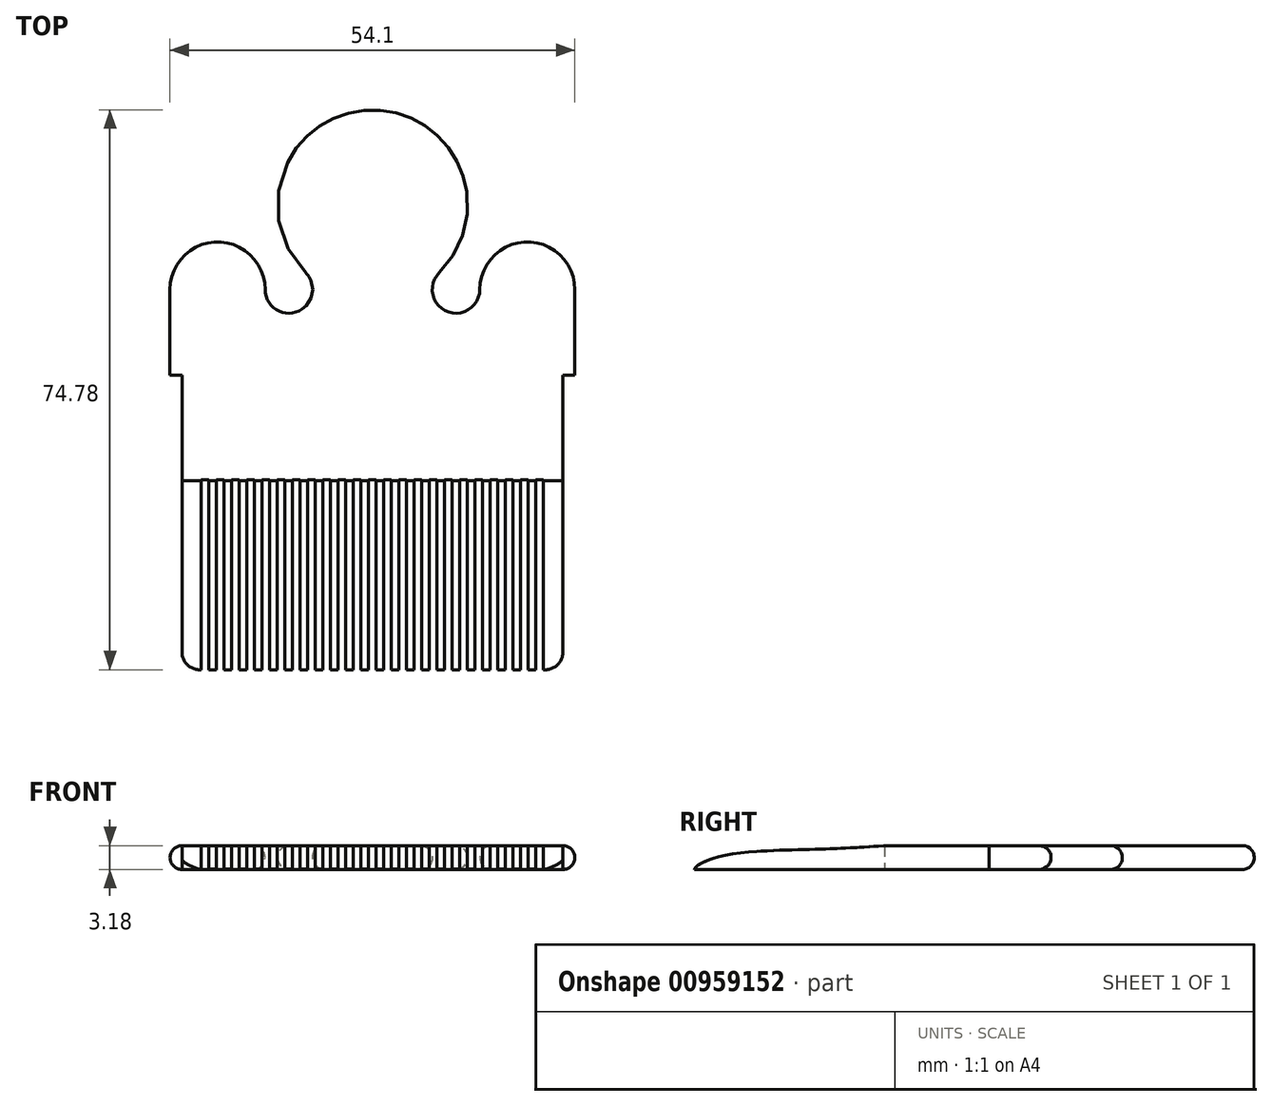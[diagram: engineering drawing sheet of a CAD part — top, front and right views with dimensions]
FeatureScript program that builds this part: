
annotation { "Feature Type Name" : "Feature", "Feature Type Description" : "" }
export const myFeature = defineFeature(function(context is Context, id is Id, definition is map)
    precondition{}
    {
        {
            var Q0;
            Q0=qCreatedBy(makeId("Top.planeOp"),FACE);
            var sketch = newSketch(context, id + "F0", { "sketchPlane" : qUnion([Q0])});
            skPoint(sketch, "E0.middle", {"position": v(0, 0) * mm});
            skArc(sketch, "E1", {"start": v(8.94, 27.66) * mm, "mid": v(0, 49.38) * mm, "end": v(-8.94, 27.66) * mm});
            skArc(sketch, "E2", {"start": v(8.94, 27.66) * mm, "mid": v(9.95, 22.47) * mm, "end": v(14.35, 25.4) * mm});
            skArc(sketch, "E3", {"start": v(-14.35, 25.4) * mm, "mid": v(-9.95, 22.47) * mm, "end": v(-8.94, 27.66) * mm});
            skArc(sketch, "E4", {"start": v(27.05, 25.4) * mm, "mid": v(20.7, 31.75) * mm, "end": v(14.35, 25.4) * mm});
            skArc(sketch, "E5", {"start": v(-14.35, 25.4) * mm, "mid": v(-20.7, 31.75) * mm, "end": v(-27.05, 25.4) * mm});
            skLineSegment(sketch, "E6.bottom", {"start": v(27.05, 25.4) * mm, "end": v(27.05, 25.4) * mm});
            skLineSegment(sketch, "E7.bottom", {"start": v(-27.05, 25.4) * mm, "end": v(-27.05, 25.4) * mm});
            skLineSegment(sketch, "E8", {"start": v(25.45, 13.97) * mm, "end": v(27.05, 13.97) * mm});
            skLineSegment(sketch, "E9", {"start": v(-25.45, 13.97) * mm, "end": v(-27.05, 13.97) * mm});
            skLineSegment(sketch, "E10.trimOffspring", {"start": v(17.78, -25.4) * mm, "end": v(16.76, -25.4) * mm});
            skLineSegment(sketch, "E11.top", {"start": v(-0.5, 0) * mm, "end": v(0.5, 0) * mm});
            skLineSegment(sketch, "E11.left", {"start": v(-0.5, -25.4) * mm, "end": v(-0.5, 0) * mm});
            skLineSegment(sketch, "E11.right", {"start": v(0.5, -25.4) * mm, "end": v(0.5, 0) * mm});
            skLineSegment(sketch, "E12.0", {"start": v(1.52, -25.4) * mm, "end": v(1.52, 0) * mm});
            skLineSegment(sketch, "E13.0", {"start": v(2.54, -25.4) * mm, "end": v(2.54, 0) * mm});
            skLineSegment(sketch, "E14.0", {"start": v(3.56, -25.4) * mm, "end": v(3.56, 0) * mm});
            skLineSegment(sketch, "E15.0", {"start": v(4.57, -25.4) * mm, "end": v(4.57, 0) * mm});
            skLineSegment(sketch, "E16.0", {"start": v(5.59, -25.4) * mm, "end": v(5.59, 0) * mm});
            skLineSegment(sketch, "E17.0", {"start": v(6.6, -25.4) * mm, "end": v(6.6, 0) * mm});
            skLineSegment(sketch, "E18.0", {"start": v(7.62, -25.4) * mm, "end": v(7.62, 0) * mm});
            skLineSegment(sketch, "E19.0", {"start": v(8.64, -25.4) * mm, "end": v(8.64, 0) * mm});
            skLineSegment(sketch, "E20.0", {"start": v(9.65, -25.4) * mm, "end": v(9.65, 0) * mm});
            skLineSegment(sketch, "E21.0", {"start": v(10.67, -25.4) * mm, "end": v(10.67, 0) * mm});
            skLineSegment(sketch, "E22.0", {"start": v(11.68, -25.4) * mm, "end": v(11.68, 0) * mm});
            skLineSegment(sketch, "E23.0", {"start": v(12.7, -25.4) * mm, "end": v(12.7, 0) * mm});
            skLineSegment(sketch, "E24.0", {"start": v(13.72, -25.4) * mm, "end": v(13.72, 0) * mm});
            skLineSegment(sketch, "E25.0", {"start": v(14.73, -25.4) * mm, "end": v(14.73, 0) * mm});
            skLineSegment(sketch, "E26.0", {"start": v(15.75, -25.4) * mm, "end": v(15.75, 0) * mm});
            skLineSegment(sketch, "E27.0", {"start": v(16.76, -25.4) * mm, "end": v(16.76, 0) * mm});
            skLineSegment(sketch, "E28.0", {"start": v(17.78, -25.4) * mm, "end": v(17.78, 0) * mm});
            skLineSegment(sketch, "E29.0", {"start": v(18.8, -25.4) * mm, "end": v(18.8, 0) * mm});
            skLineSegment(sketch, "E30.0", {"start": v(19.81, -25.4) * mm, "end": v(19.81, 0) * mm});
            skLineSegment(sketch, "E31.0", {"start": v(20.83, -25.4) * mm, "end": v(20.83, 0) * mm});
            skLineSegment(sketch, "E32.0", {"start": v(21.84, -25.4) * mm, "end": v(21.84, 0) * mm});
            skLineSegment(sketch, "E33.0", {"start": v(22.83, -25.4) * mm, "end": v(22.83, 0) * mm});
            skLineSegment(sketch, "E34.trimOffspring", {"start": v(15.75, -25.4) * mm, "end": v(14.73, -25.4) * mm});
            skLineSegment(sketch, "E35.trimOffspring", {"start": v(13.72, -25.4) * mm, "end": v(12.7, -25.4) * mm});
            skLineSegment(sketch, "E36.trimOffspring", {"start": v(11.68, -25.4) * mm, "end": v(10.67, -25.4) * mm});
            skLineSegment(sketch, "E37.trimOffspring", {"start": v(9.65, -25.4) * mm, "end": v(8.64, -25.4) * mm});
            skLineSegment(sketch, "E38.trimOffspring", {"start": v(7.62, -25.4) * mm, "end": v(6.6, -25.4) * mm});
            skLineSegment(sketch, "E39.trimOffspring", {"start": v(5.59, -25.4) * mm, "end": v(4.57, -25.4) * mm});
            skLineSegment(sketch, "E40.trimOffspring", {"start": v(3.56, -25.4) * mm, "end": v(2.54, -25.4) * mm});
            skLineSegment(sketch, "E41.trimOffspring", {"start": v(1.52, -25.4) * mm, "end": v(0.5, -25.4) * mm});
            skLineSegment(sketch, "E42.trimOffspring", {"start": v(-0.5, -25.4) * mm, "end": v(-1.52, -25.4) * mm});
            skLineSegment(sketch, "E43", {"start": v(1.52, 0) * mm, "end": v(2.54, 0) * mm});
            skLineSegment(sketch, "E44", {"start": v(3.56, 0) * mm, "end": v(4.57, 0) * mm});
            skLineSegment(sketch, "E45", {"start": v(5.59, 0) * mm, "end": v(6.6, 0) * mm});
            skLineSegment(sketch, "E46", {"start": v(7.62, 0) * mm, "end": v(8.64, 0) * mm});
            skLineSegment(sketch, "E47", {"start": v(9.65, 0) * mm, "end": v(10.67, 0) * mm});
            skLineSegment(sketch, "E48", {"start": v(11.68, 0) * mm, "end": v(12.7, 0) * mm});
            skLineSegment(sketch, "E49", {"start": v(13.72, 0) * mm, "end": v(14.73, 0) * mm});
            skLineSegment(sketch, "E50", {"start": v(15.75, 0) * mm, "end": v(16.76, 0) * mm});
            skLineSegment(sketch, "E51", {"start": v(17.78, 0) * mm, "end": v(18.8, 0) * mm});
            skLineSegment(sketch, "E52", {"start": v(19.81, 0) * mm, "end": v(20.83, 0) * mm});
            skLineSegment(sketch, "E53.0", {"start": v(-1.52, -25.4) * mm, "end": v(-1.52, 0) * mm});
            skLineSegment(sketch, "E54.0", {"start": v(-2.54, -25.4) * mm, "end": v(-2.54, 0) * mm});
            skLineSegment(sketch, "E55.0", {"start": v(-3.56, -25.4) * mm, "end": v(-3.56, 0) * mm});
            skLineSegment(sketch, "E56.0", {"start": v(-4.57, -25.4) * mm, "end": v(-4.57, 0) * mm});
            skLineSegment(sketch, "E57.0", {"start": v(-5.59, -25.4) * mm, "end": v(-5.59, 0) * mm});
            skLineSegment(sketch, "E58.trimOffspring", {"start": v(-2.54, -25.4) * mm, "end": v(-3.56, -25.4) * mm});
            skLineSegment(sketch, "E59.trimOffspring", {"start": v(-4.57, -25.4) * mm, "end": v(-5.59, -25.4) * mm});
            skLineSegment(sketch, "E60", {"start": v(-4.57, 0) * mm, "end": v(-3.56, 0) * mm});
            skLineSegment(sketch, "E61", {"start": v(-2.54, 0) * mm, "end": v(-1.52, 0) * mm});
            skLineSegment(sketch, "E62.MirrorCS", {"start": v(-6.6, -25.4) * mm, "end": v(-6.6, 0) * mm});
            skLineSegment(sketch, "E63.MirrorCS", {"start": v(-7.62, -25.4) * mm, "end": v(-7.62, 0) * mm});
            skLineSegment(sketch, "E64.MirrorCS", {"start": v(-8.64, -25.4) * mm, "end": v(-8.64, 0) * mm});
            skLineSegment(sketch, "E65.MirrorCS", {"start": v(-9.65, -25.4) * mm, "end": v(-9.65, 0) * mm});
            skLineSegment(sketch, "E66.MirrorCS", {"start": v(-10.67, -25.4) * mm, "end": v(-10.67, 0) * mm});
            skLineSegment(sketch, "E67.MirrorCS", {"start": v(-11.68, -25.4) * mm, "end": v(-11.68, 0) * mm});
            skLineSegment(sketch, "E68.MirrorCS", {"start": v(-12.7, -25.4) * mm, "end": v(-12.7, 0) * mm});
            skLineSegment(sketch, "E69.MirrorCS", {"start": v(-13.72, -25.4) * mm, "end": v(-13.72, 0) * mm});
            skLineSegment(sketch, "E70.MirrorCS", {"start": v(-14.73, -25.4) * mm, "end": v(-14.73, 0) * mm});
            skLineSegment(sketch, "E71.MirrorCS", {"start": v(-15.75, -25.4) * mm, "end": v(-15.75, 0) * mm});
            skLineSegment(sketch, "E72.MirrorCS", {"start": v(-16.76, -25.4) * mm, "end": v(-16.76, 0) * mm});
            skLineSegment(sketch, "E73.MirrorCS", {"start": v(-17.78, -25.4) * mm, "end": v(-17.78, 0) * mm});
            skLineSegment(sketch, "E74.MirrorCS", {"start": v(-18.8, -25.4) * mm, "end": v(-18.8, 0) * mm});
            skLineSegment(sketch, "E75.MirrorCS", {"start": v(-19.81, -25.4) * mm, "end": v(-19.81, 0) * mm});
            skLineSegment(sketch, "E76.MirrorCS", {"start": v(-20.83, -25.4) * mm, "end": v(-20.83, 0) * mm});
            skLineSegment(sketch, "E77.MirrorCS", {"start": v(-21.84, -25.4) * mm, "end": v(-21.84, 0) * mm});
            skLineSegment(sketch, "E78.trimOffspring", {"start": v(-6.6, -25.4) * mm, "end": v(-7.62, -25.4) * mm});
            skLineSegment(sketch, "E79.trimOffspring", {"start": v(-8.64, -25.4) * mm, "end": v(-9.65, -25.4) * mm});
            skLineSegment(sketch, "E80.trimOffspring", {"start": v(-10.67, -25.4) * mm, "end": v(-11.68, -25.4) * mm});
            skLineSegment(sketch, "E81.trimOffspring", {"start": v(-12.7, -25.4) * mm, "end": v(-13.72, -25.4) * mm});
            skLineSegment(sketch, "E82.trimOffspring", {"start": v(-14.73, -25.4) * mm, "end": v(-15.75, -25.4) * mm});
            skLineSegment(sketch, "E83.trimOffspring", {"start": v(-16.76, -25.4) * mm, "end": v(-17.78, -25.4) * mm});
            skLineSegment(sketch, "E84", {"start": v(-20.83, 0) * mm, "end": v(-19.81, 0) * mm});
            skLineSegment(sketch, "E85", {"start": v(-18.8, 0) * mm, "end": v(-17.78, 0) * mm});
            skLineSegment(sketch, "E86", {"start": v(-16.76, 0) * mm, "end": v(-15.75, 0) * mm});
            skLineSegment(sketch, "E87", {"start": v(-14.73, 0) * mm, "end": v(-13.72, 0) * mm});
            skLineSegment(sketch, "E88", {"start": v(-12.7, 0) * mm, "end": v(-11.68, 0) * mm});
            skLineSegment(sketch, "E89", {"start": v(-10.67, 0) * mm, "end": v(-9.65, 0) * mm});
            skLineSegment(sketch, "E90", {"start": v(-8.64, 0) * mm, "end": v(-7.62, 0) * mm});
            skLineSegment(sketch, "E91", {"start": v(-6.6, 0) * mm, "end": v(-5.59, 0) * mm});
            skLineSegment(sketch, "E92.MirrorCS", {"start": v(-22.86, -25.4) * mm, "end": v(-22.86, 0) * mm});
            skLineSegment(sketch, "E93", {"start": v(-22.86, 0) * mm, "end": v(-21.84, 0) * mm});
            skLineSegment(sketch, "E94", {"start": v(18.8, -25.4) * mm, "end": v(19.81, -25.4) * mm});
            skLineSegment(sketch, "E95", {"start": v(20.83, -25.4) * mm, "end": v(21.84, -25.4) * mm});
            skLineSegment(sketch, "E96", {"start": v(-21.84, -25.4) * mm, "end": v(-20.83, -25.4) * mm});
            skLineSegment(sketch, "E97", {"start": v(-19.81, -25.4) * mm, "end": v(-18.8, -25.4) * mm});
            skLineSegment(sketch, "E98", {"start": v(-22.86, -25.4) * mm, "end": v(-23.08, -25.4) * mm});
            skLineSegment(sketch, "E99", {"start": v(-25.45, 13.97) * mm, "end": v(-25.45, -23.04) * mm});
            skLineSegment(sketch, "E100", {"start": v(22.83, -25.4) * mm, "end": v(23.08, -25.4) * mm});
            skLineSegment(sketch, "E101", {"start": v(25.45, 13.97) * mm, "end": v(25.45, -23.04) * mm});
            skLineSegment(sketch, "E102", {"start": v(21.84, 0) * mm, "end": v(22.83, 0) * mm});
            skLineSegment(sketch, "E103", {"start": v(-27.05, 25.4) * mm, "end": v(-27.05, 13.97) * mm});
            skLineSegment(sketch, "E104", {"start": v(27.05, 25.4) * mm, "end": v(27.05, 13.97) * mm});
            skPoint(sketch, "E105.visualSharp", {"position": v(-25.45, -25.4) * mm});
            skArc(sketch, "E105.filletArc", {"start": v(-25.45, -23.04) * mm, "mid": v(-24.76, -24.7) * mm, "end": v(-23.08, -25.4) * mm});
            skPoint(sketch, "E106.visualSharp", {"position": v(25.45, -25.4) * mm});
            skArc(sketch, "E106.filletArc", {"start": v(23.08, -25.4) * mm, "mid": v(24.76, -24.7) * mm, "end": v(25.45, -23.04) * mm});
            skSolve(sketch);
        }
        {
            var Q0;
            Q0 = qSketchRegion(id + "F0", true);
            extrude(context, id + "F1", {"entities" : qUnion([Q0]), "depth" : 3.17 * mm, "offsetDistance" : 25.4 * mm});
        }
        {
            var Q0;
            Q0=makeQuery(id+"F1.opExtrude","SWEPT_FACE",FACE,{"disambiguationData":[OSD([sQuery(id+"F0.wireOp",EDGE,"E1")])]});
            fillet(context, id + "F2", {"entities" : qUnion([Q0]), "radius" : 1.59 * mm, "tangentPropagation" : true, "allowEdgeOverflow" : false});
        }
        {
            var Q0;
            Q0=qCreatedBy(makeId("Right.planeOp"),FACE);
            var sketch = newSketch(context, id + "F3", { "sketchPlane" : qUnion([Q0])});
            skLineSegment(sketch, "E107", {"start": v(-25.4, 0) * mm, "end": v(-25.4, 3.19) * mm});
            skLineSegment(sketch, "E108", {"start": v(-25.4, 3.19) * mm, "end": v(0, 3.19) * mm});
            skLineSegment(sketch, "E109", {"start": v(0, 3.19) * mm, "end": v(0, 0.33) * mm});
            skLineSegment(sketch, "E110", {"start": v(-25.4, 0) * mm, "end": v(-25.4, 0) * mm});
            skFitSpline(sketch, "E111", {"points": [v(0, 3.19) * mm, v(-9.48, 2.7) * mm, v(-22.57, 1.58) * mm, v(-25.4, 0) * mm, v(-24.57, 0) * mm], "startDerivative": vector(-29.93, -2.14) * mm, "endDerivative": vector(14.28, 9) * mm});
            skSolve(sketch);
        }
        {
            var Q0;
            Q0 = qSketchRegion(id + "F3", true);
            extrude(context, id + "F4", {"entities" : qUnion([Q0]), "operationType" : NewBodyOperationType.REMOVE, "endBound" : BoundingType.SYMMETRIC, "oppositeDirection" : true, "depth" : 57.15 * mm, "offsetDistance" : 25.4 * mm});
        }
    });
